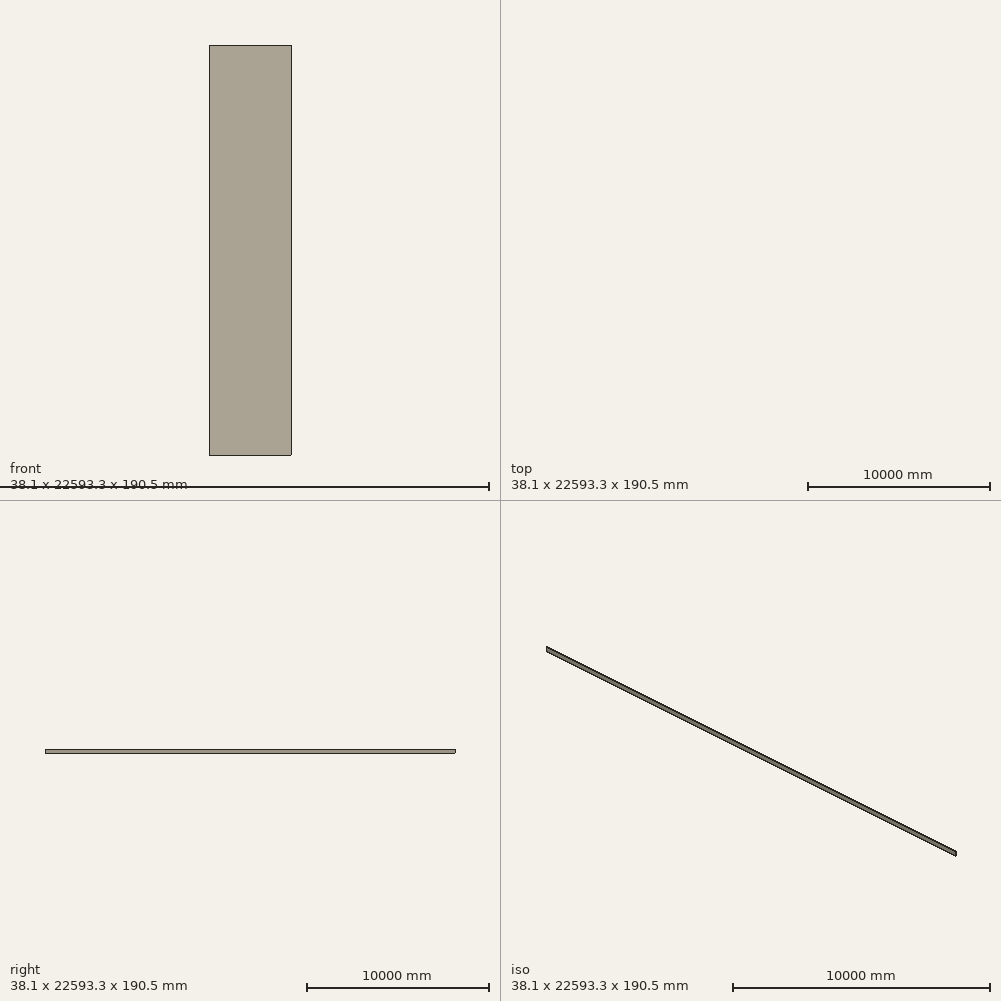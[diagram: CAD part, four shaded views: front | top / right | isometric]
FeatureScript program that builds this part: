
annotation { "Feature Type Name" : "Feature", "Feature Type Description" : "" }
export const myFeature = defineFeature(function(context is Context, id is Id, definition is map)
    precondition{}
    {
        {
            var Q0;
            Q0=qCreatedBy(makeId("Front.planeOp"),FACE);
            var sketch = newSketch(context, id + "F0", { "sketchPlane" : qUnion([Q0])});
            skLineSegment(sketch, "E0.bottom", {"start": v(0, 0) * mm, "end": v(38.1, 0) * mm});
            skLineSegment(sketch, "E0.top", {"start": v(0, 190.5) * mm, "end": v(38.1, 190.5) * mm});
            skLineSegment(sketch, "E0.left", {"start": v(0, 0) * mm, "end": v(0, 190.5) * mm});
            skLineSegment(sketch, "E0.right", {"start": v(38.1, 0) * mm, "end": v(38.1, 190.5) * mm});
            skSolve(sketch);
        }
        {
            var Q0;
            Q0 = qSketchRegion(id + "F0", true);
            extrude(context, id + "F1", {"entities" : qUnion([Q0]), "depth" : 22593.3 * mm});
        }
    });
